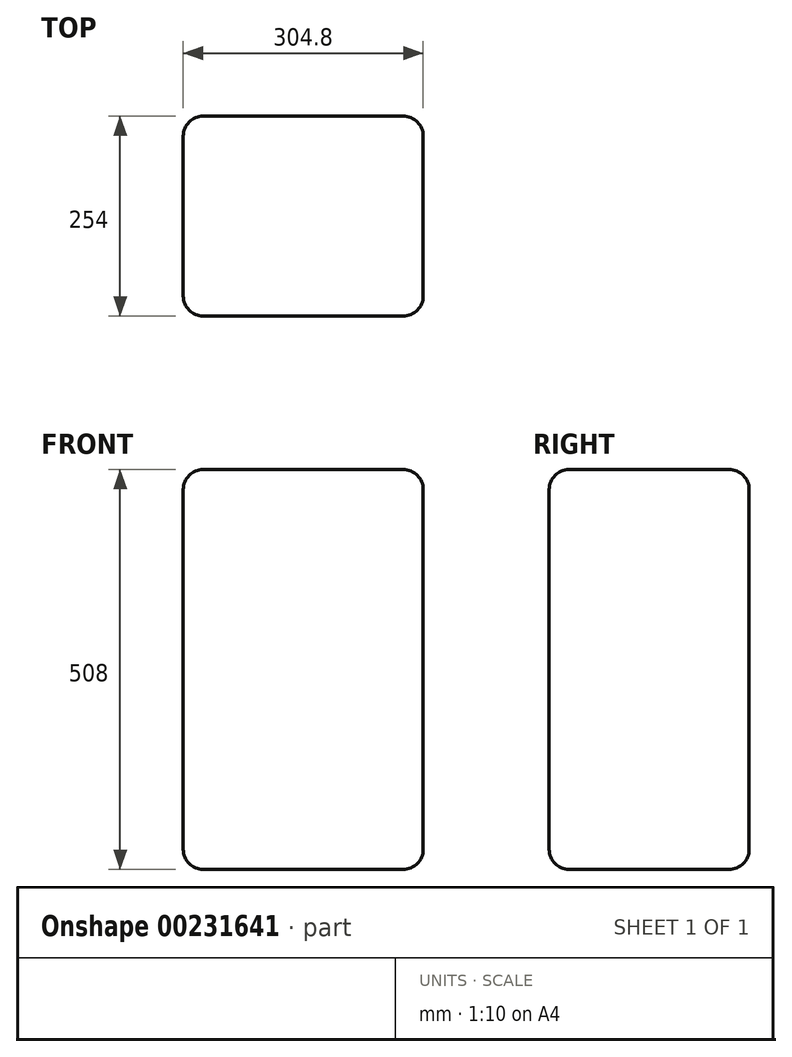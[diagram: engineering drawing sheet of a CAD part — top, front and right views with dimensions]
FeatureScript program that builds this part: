
annotation { "Feature Type Name" : "Feature", "Feature Type Description" : "" }
export const myFeature = defineFeature(function(context is Context, id is Id, definition is map)
    precondition{}
    {
        {
            var Q0;
            Q0=qCreatedBy(makeId("Front.planeOp"),FACE);
            var sketch = newSketch(context, id + "F0", { "sketchPlane" : qUnion([Q0])});
            skLineSegment(sketch, "E0.bottom", {"start": v(152.4, 254) * mm, "end": v(-152.4, 254) * mm});
            skLineSegment(sketch, "E0.top", {"start": v(152.4, -254) * mm, "end": v(-152.4, -254) * mm});
            skLineSegment(sketch, "E0.left", {"start": v(152.4, 254) * mm, "end": v(152.4, -254) * mm});
            skLineSegment(sketch, "E0.right", {"start": v(-152.4, 254) * mm, "end": v(-152.4, -254) * mm});
            skPoint(sketch, "E0.middle", {"position": v(0, 0) * mm});
            skSolve(sketch);
        }
        {
            var Q0;
            Q0 = qSketchRegion(id + "F0", true);
            extrude(context, id + "F1", {"entities" : qUnion([Q0]), "depth" : 254 * mm});
        }
        {
            var Q0;
            Q0=makeQuery(id+"F1.opExtrude","CAP_EDGE",EDGE,{"disambiguationData":[OSD([sQuery(id+"F0.wireOp",EDGE,"E0.right")])],"isStart":false});
            var Q1;
            Q1=makeQuery(id+"F1.opExtrude","CAP_EDGE",EDGE,{"disambiguationData":[OSD([sQuery(id+"F0.wireOp",EDGE,"E0.bottom")])],"isStart":false});
            var Q2;
            Q2=makeQuery(id+"F1.opExtrude","CAP_EDGE",EDGE,{"disambiguationData":[OSD([sQuery(id+"F0.wireOp",EDGE,"E0.left")])],"isStart":false});
            var Q3;
            Q3=makeQuery(id+"F1.opExtrude","CAP_EDGE",EDGE,{"disambiguationData":[OSD([sQuery(id+"F0.wireOp",EDGE,"E0.top")])],"isStart":false});
            var Q4;
            Q4=makeQuery(id+"F1.opExtrude","SWEPT_EDGE",EDGE,{"disambiguationData":[OSD([sQuery(id+"F0.wireOp",EDGE,"E0.top"),sQuery(id+"F0.wireOp",EDGE,"E0.right")])]});
            var Q5;
            Q5=makeQuery(id+"F1.opExtrude","SWEPT_EDGE",EDGE,{"disambiguationData":[OSD([sQuery(id+"F0.wireOp",EDGE,"E0.bottom"),sQuery(id+"F0.wireOp",EDGE,"E0.right")])]});
            var Q6;
            Q6=makeQuery(id+"F1.opExtrude","SWEPT_EDGE",EDGE,{"disambiguationData":[OSD([sQuery(id+"F0.wireOp",EDGE,"E0.bottom"),sQuery(id+"F0.wireOp",EDGE,"E0.left")])]});
            var Q7;
            Q7=makeQuery(id+"F1.opExtrude","SWEPT_EDGE",EDGE,{"disambiguationData":[OSD([sQuery(id+"F0.wireOp",EDGE,"E0.top"),sQuery(id+"F0.wireOp",EDGE,"E0.left")])]});
            var Q8;
            Q8=makeQuery(id+"F1.opExtrude","CAP_EDGE",EDGE,{"disambiguationData":[OSD([sQuery(id+"F0.wireOp",EDGE,"E0.top")])],"isStart":true});
            var Q9;
            Q9=makeQuery(id+"F1.opExtrude","CAP_EDGE",EDGE,{"disambiguationData":[OSD([sQuery(id+"F0.wireOp",EDGE,"E0.left")])],"isStart":true});
            var Q10;
            Q10=makeQuery(id+"F1.opExtrude","CAP_EDGE",EDGE,{"disambiguationData":[OSD([sQuery(id+"F0.wireOp",EDGE,"E0.bottom")])],"isStart":true});
            var Q11;
            Q11=makeQuery(id+"F1.opExtrude","CAP_EDGE",EDGE,{"disambiguationData":[OSD([sQuery(id+"F0.wireOp",EDGE,"E0.right")])],"isStart":true});
            fillet(context, id + "F2", {"entities" : qUnion([Q0, Q1, Q2, Q3, Q4, Q5, Q6, Q7, Q8, Q9, Q10, Q11]), "radius" : 25.4 * mm, "tangentPropagation" : true, "allowEdgeOverflow" : false});
        }
    });
